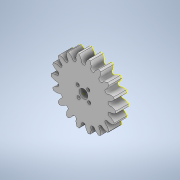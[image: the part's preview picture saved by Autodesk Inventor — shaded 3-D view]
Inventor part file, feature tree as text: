
AUTODESK INVENTOR PART (.ipt)
format: ipt  version: 2021 (Build 250183000, 183)  size: 414,720 bytes
history: native  units: in
note: dims shown in document units (in); Inventor stores cm internally (conversion verified against a paired STEP export)
features: sketch x3, extrude x3, projected_geometry x1
ambient origin geometry x8: Origin, YZ Plane, XZ Plane, XY Plane, X Axis, Y Axis, Z Axis, Center Point
bodies: Solid2 (feature_tree), Solid1 (feature_tree)
feature tree (7):
  sketch  "Sketch1"  dims[d0=0.3937in d1=0.0in d2=0.4724in d3=0.0in]
  extrude  "Extrusion1"  Depth=0.4724in TaperAngle=0.0deg
  extrude  "Extrusion2"  Depth=0.1181in
  extrude  "Extrusion3"  Depth=0.1181in
  sketch  "Sketch4"  dims[d8=0.2756in d9=0.1181in d10=0.2756in d11=0.1181in d12=0.2756in d13=0.0in d14=0.0in d26=0.0197in d27=1.9685in d28=0.0197in d29=1.9685in]
  projected_geometry  "Projected Loop1"
  sketch  "Sketch2"  dims[d4=0.315in d7=0.1181in]
